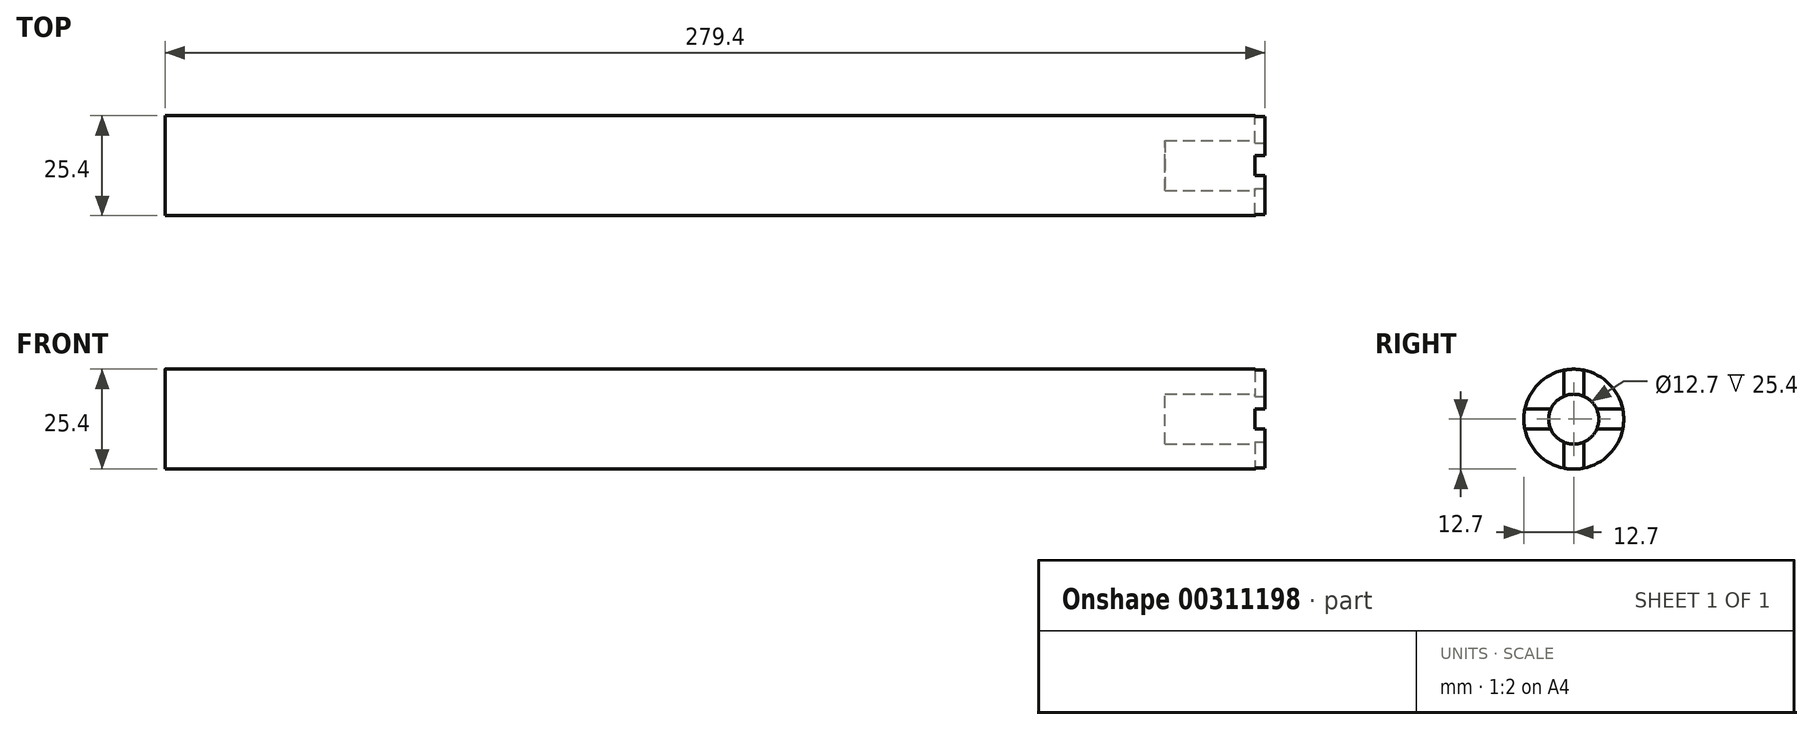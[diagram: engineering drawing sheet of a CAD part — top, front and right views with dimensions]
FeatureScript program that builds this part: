
annotation { "Feature Type Name" : "Feature", "Feature Type Description" : "" }
export const myFeature = defineFeature(function(context is Context, id is Id, definition is map)
    precondition{}
    {
        {
            var Q0;
            Q0=qCreatedBy(makeId("Right.planeOp"),FACE);
            var sketch = newSketch(context, id + "F0", { "sketchPlane" : qUnion([Q0])});
            skCircle(sketch, "E0", {"center": v(0, 0) * mm, "radius": 12.7 * mm});
            skSolve(sketch);
        }
        {
            var Q0;
            Q0 = qSketchRegion(id + "F0", true);
            extrude(context, id + "F1", {"entities" : qUnion([Q0]), "depth" : 279.4 * mm});
        }
        {
            var Q0;
            Q0=makeQuery(id+"F1.opExtrude","CAP_FACE",FACE,{"disambiguationData":[OSD([sQuery(id+"F0.wireOp",EDGE,"E0")])],"isStart":false});
            var sketch = newSketch(context, id + "F2", { "sketchPlane" : qUnion([Q0])});
            skCircle(sketch, "E1", {"center": v(0, 0) * mm, "radius": 6.35 * mm});
            skSolve(sketch);
        }
        {
            var Q0;
            Q0 = qSketchRegion(id + "F2", true);
            extrude(context, id + "F3", {"entities" : qUnion([Q0]), "operationType" : NewBodyOperationType.REMOVE, "oppositeDirection" : true, "depth" : 25.4 * mm});
        }
        {
            var Q0;
            Q0=makeQuery(id+"F1.opExtrude","CAP_FACE",FACE,{"disambiguationData":[OSD([sQuery(id+"F0.wireOp",EDGE,"E0")])],"isStart":false});
            var sketch = newSketch(context, id + "F4", { "sketchPlane" : qUnion([Q0])});
            skLineSegment(sketch, "E2.0", {"start": v(-12.7, 2.54) * mm, "end": v(12.7, 2.54) * mm});
            skLineSegment(sketch, "E3.0", {"start": v(-12.7, -2.54) * mm, "end": v(12.7, -2.54) * mm});
            skLineSegment(sketch, "E4", {"start": v(-12.7, 2.54) * mm, "end": v(-12.7, -2.54) * mm});
            skLineSegment(sketch, "E5", {"start": v(12.7, 2.54) * mm, "end": v(12.7, -2.54) * mm});
            skPoint(sketch, "E6.endSnap0", {"position": v(0, -2.54) * mm});
            skLineSegment(sketch, "E7.0", {"start": v(-2.54, 12.7) * mm, "end": v(-2.54, -12.7) * mm});
            skLineSegment(sketch, "E8.0", {"start": v(2.54, 12.7) * mm, "end": v(2.54, -12.7) * mm});
            skLineSegment(sketch, "E9", {"start": v(-2.54, -12.7) * mm, "end": v(2.54, -12.7) * mm});
            skLineSegment(sketch, "E10", {"start": v(-2.54, 12.7) * mm, "end": v(2.54, 12.7) * mm});
            skSolve(sketch);
        }
        {
            var Q0;
            Q0 = qSketchRegion(id + "F4", true);
            extrude(context, id + "F5", {"entities" : qUnion([Q0]), "operationType" : NewBodyOperationType.REMOVE, "oppositeDirection" : true, "depth" : 2.54 * mm});
        }
    });
